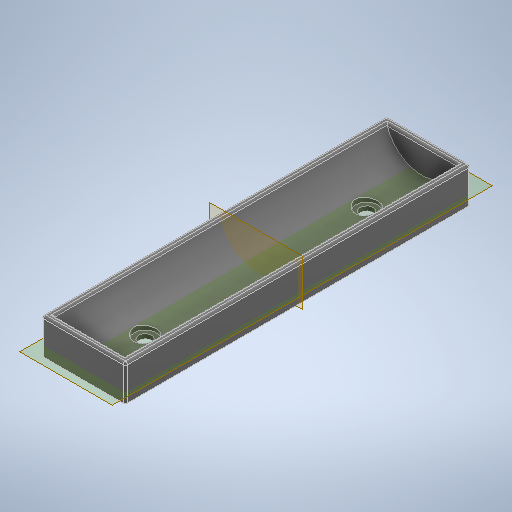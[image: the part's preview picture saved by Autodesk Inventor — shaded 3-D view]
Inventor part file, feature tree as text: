
AUTODESK INVENTOR PART (.ipt)
format: ipt  version: 2025.1 (Build 291241020, 241B)  size: 672,256 bytes
history: native  units: mm
features: sketch x3, extrude x2, plane x2, mirror x1, fillet x1, hole x1
ambient origin geometry x8: Origin, YZ Plane, XZ Plane, XY Plane, X Axis, Y Axis, Z Axis, Center Point
bodies: Body1 (feature_tree)
feature tree (10):
  extrude  "Extrusion3"  Depth=20.0mm
  plane  "Work Plane1"
  extrude  "Extrusion4"  Depth=3.0mm
  mirror  "Mirror1"
  fillet  "Fillet1"  Radius=3.0mm
  plane  "Work Plane2"
  hole  "Hole1"  [1 undecoded]
  sketch  "Sketch3"  dims[d6=16.5mm d9=20.0mm]
  sketch  "Sketch4"  dims[d10=150.0mm d11=0.0mm d12=38.0mm d13=3.0mm]
  sketch  "Sketch5"  dims[d14=3.0mm d16=1.0mm d17=3.0mm d18=0.0mm d19=-4.5mm d20=19.0mm d21=100.0mm d22=28.0mm d23=28.0mm d24=6.0mm d25=6.0mm d26=10.0mm d27=2.5mm d28=90.0deg d29=8.0mm d30=20.594885mm]
note: 1 required parameter value undecoded (feature->parameter linkage not recoverable at this tier; creation-order binding heuristic only, values carry confidence <= 0.55)
